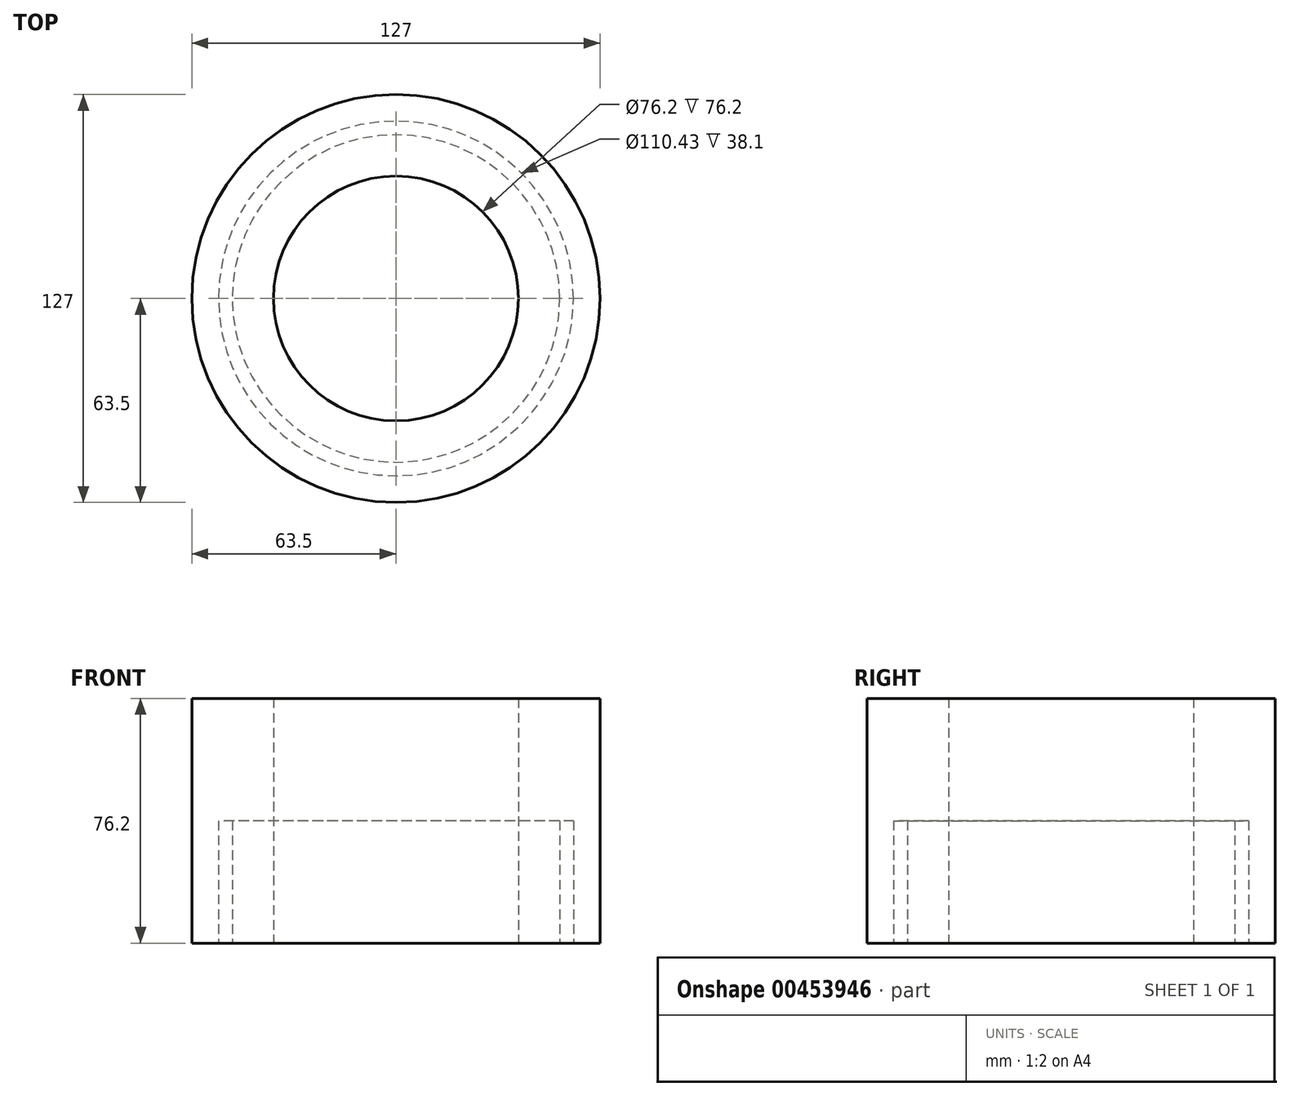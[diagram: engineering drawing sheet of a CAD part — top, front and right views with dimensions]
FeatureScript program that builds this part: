
annotation { "Feature Type Name" : "Feature", "Feature Type Description" : "" }
export const myFeature = defineFeature(function(context is Context, id is Id, definition is map)
    precondition{}
    {
        {
            var Q0;
            Q0=qCreatedBy(makeId("Top.planeOp"),FACE);
            var sketch = newSketch(context, id + "F0", { "sketchPlane" : qUnion([Q0])});
            skCircle(sketch, "E0", {"center": v(0, 0) * mm, "radius": 63.5 * mm});
            skCircle(sketch, "E1", {"center": v(0, 0) * mm, "radius": 38.1 * mm});
            skSolve(sketch);
        }
        {
            var Q0;
            Q0 = qSketchRegion(id + "F0", true);
            extrude(context, id + "F1", {"entities" : qUnion([Q0]), "depth" : 76.2 * mm});
        }
        {
            var Q0;
            Q0=qCreatedBy(makeId("Top.planeOp"),FACE);
            var sketch = newSketch(context, id + "F2", { "sketchPlane" : qUnion([Q0])});
            skCircle(sketch, "E2", {"center": v(0, 0) * mm, "radius": 55.21 * mm});
            skCircle(sketch, "E3", {"center": v(0, 0) * mm, "radius": 50.95 * mm});
            skSolve(sketch);
        }
        {
            var Q0;
            Q0 = qSketchRegion(id + "F2", true);
            extrude(context, id + "F3", {"entities" : qUnion([Q0]), "operationType" : NewBodyOperationType.REMOVE, "depth" : 38.1 * mm});
        }
    });
